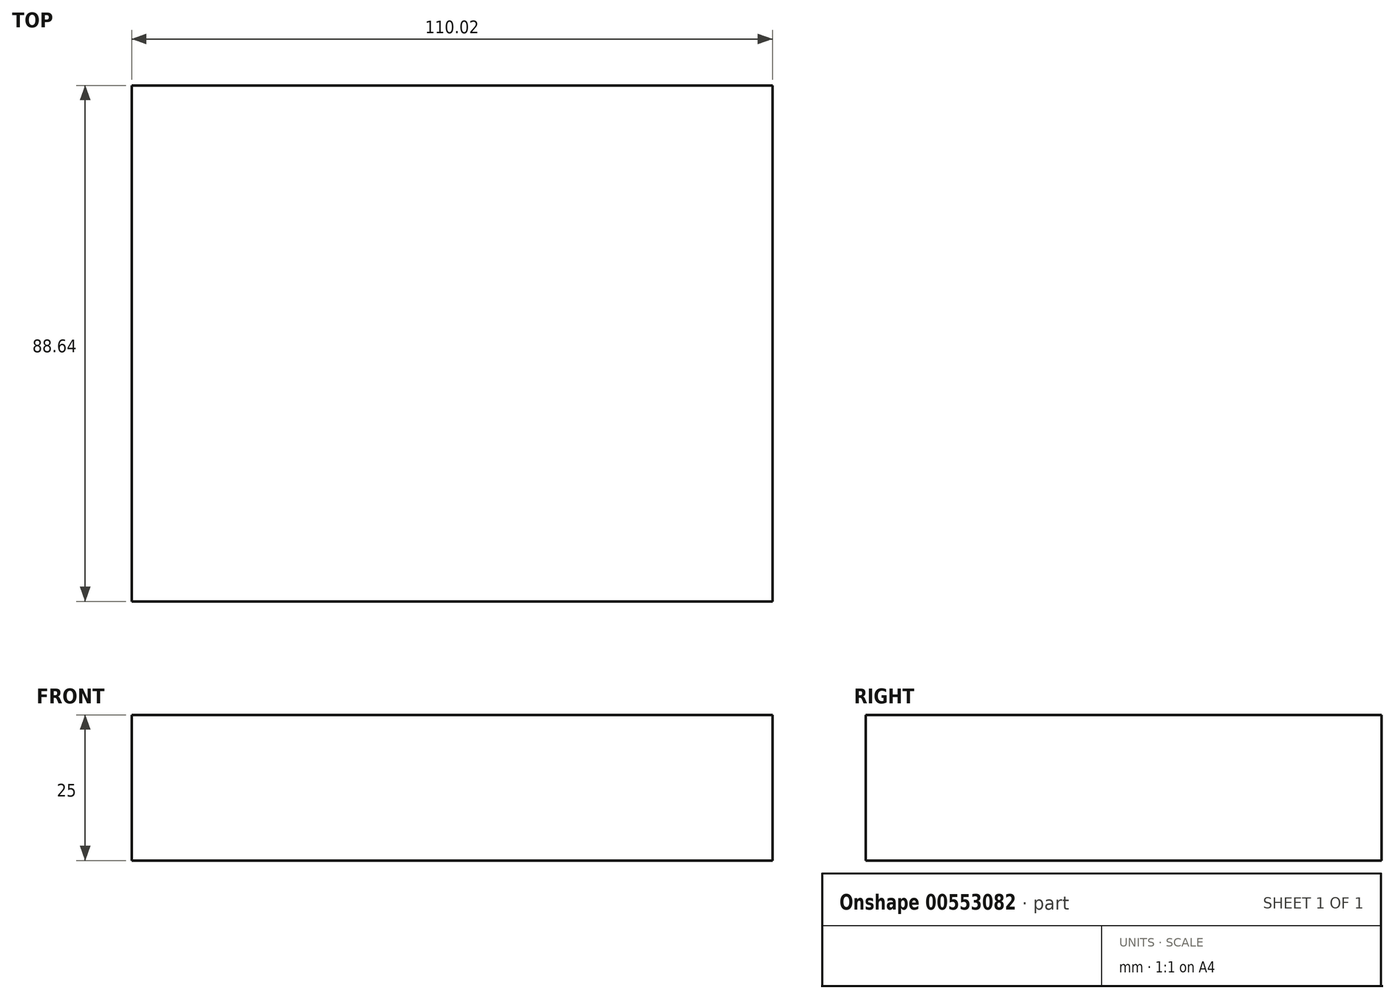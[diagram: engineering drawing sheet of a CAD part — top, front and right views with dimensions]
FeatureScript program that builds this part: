
annotation { "Feature Type Name" : "Feature", "Feature Type Description" : "" }
export const myFeature = defineFeature(function(context is Context, id is Id, definition is map)
    precondition{}
    {
        {
            var Q0;
            Q0=qCreatedBy(makeId("Top.planeOp"),FACE);
            var sketch = newSketch(context, id + "F0", { "sketchPlane" : qUnion([Q0])});
            skLineSegment(sketch, "E0.bottom", {"start": v(0, 0) * mm, "end": v(110.02, 0) * mm});
            skLineSegment(sketch, "E0.top", {"start": v(0, -88.64) * mm, "end": v(110.02, -88.64) * mm});
            skLineSegment(sketch, "E0.left", {"start": v(0, 0) * mm, "end": v(0, -88.64) * mm});
            skLineSegment(sketch, "E0.right", {"start": v(110.02, 0) * mm, "end": v(110.02, -88.64) * mm});
            skSolve(sketch);
        }
        {
            var Q0;
            Q0 = qSketchRegion(id + "F0", true);
            extrude(context, id + "F1", {"entities" : qUnion([Q0]), "depth" : 25 * mm, "offsetDistance" : 25 * mm});
        }
    });
